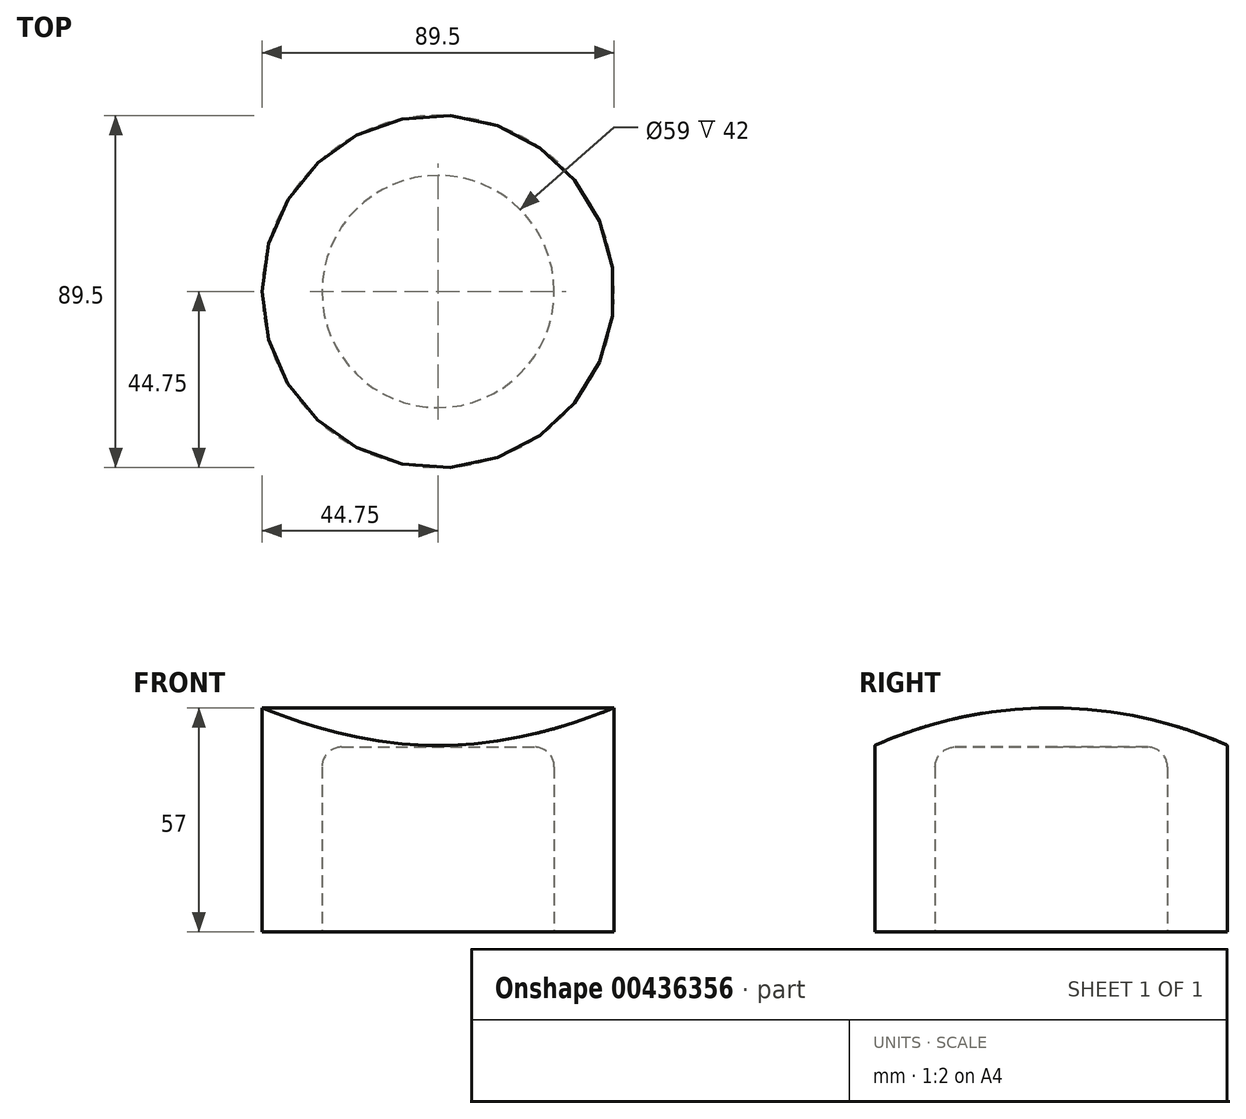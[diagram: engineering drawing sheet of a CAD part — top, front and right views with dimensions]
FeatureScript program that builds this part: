
annotation { "Feature Type Name" : "Feature", "Feature Type Description" : "" }
export const myFeature = defineFeature(function(context is Context, id is Id, definition is map)
    precondition{}
    {
        {
            var Q0;
            Q0=qCreatedBy(makeId("Front.planeOp"),FACE);
            var sketch = newSketch(context, id + "F0", { "sketchPlane" : qUnion([Q0])});
            skLineSegment(sketch, "E0", {"start": v(0, 0) * mm, "end": v(44.75, 0) * mm});
            skLineSegment(sketch, "E1", {"start": v(44.75, 0) * mm, "end": v(44.75, -57) * mm});
            skLineSegment(sketch, "E2", {"start": v(44.75, -57) * mm, "end": v(29.5, -57) * mm});
            skLineSegment(sketch, "E3", {"start": v(29.5, -57) * mm, "end": v(29.5, -48) * mm});
            skLineSegment(sketch, "E4", {"start": v(29.5, -48) * mm, "end": v(35.5, -48) * mm});
            skLineSegment(sketch, "E5", {"start": v(35.5, -51.58) * mm, "end": v(35.5, -48) * mm});
            skLineSegment(sketch, "E6", {"start": v(35.5, -51.58) * mm, "end": v(29.5, -51.58) * mm});
            skLineSegment(sketch, "E7", {"start": v(29.5, -51.58) * mm, "end": v(29.5, -15) * mm});
            skLineSegment(sketch, "E8", {"start": v(24.5, -10) * mm, "end": v(0, -10) * mm});
            skLineSegment(sketch, "E9", {"start": v(0, -10) * mm, "end": v(0, 0) * mm});
            skPoint(sketch, "E10.visualSharp", {"position": v(29.5, -10) * mm});
            skArc(sketch, "E10.filletArc", {"start": v(29.5, -15) * mm, "mid": v(28.04, -11.46) * mm, "end": v(24.5, -10) * mm});
            skSolve(sketch);
        }
        {
            var Q0;
            Q0 = qSketchRegion(id + "F0", true);
            var Q1;
            Q1=sQuery(id+"F0.wireOp",EDGE,"E9");
            revolve(context, id + "F1", {"entities" : qUnion([Q0]), "axis" : qUnion([Q1]), "revolveType" : RevolveType.FULL});
        }
        {
            var Q0;
            Q0=qCreatedBy(makeId("Right.planeOp"),FACE);
            var sketch = newSketch(context, id + "F2", { "sketchPlane" : qUnion([Q0])});
            skArc(sketch, "E11", {"start": v(-45.72, -10) * mm, "mid": v(0, 0) * mm, "end": v(45.72, -10) * mm});
            skLineSegment(sketch, "E12", {"start": v(-45.72, 0) * mm, "end": v(45.72, 0) * mm, "construction": true});
            skLineSegment(sketch, "E13", {"start": v(-45.72, -10) * mm, "end": v(-45.72, 10) * mm});
            skLineSegment(sketch, "E14", {"start": v(-45.72, 10) * mm, "end": v(45.72, 10) * mm});
            skLineSegment(sketch, "E15", {"start": v(45.72, 10) * mm, "end": v(45.72, -10) * mm});
            skLineSegment(sketch, "E16", {"start": v(0, 0) * mm, "end": v(0, 10) * mm, "construction": true});
            skSolve(sketch);
        }
        {
            var Q0;
            Q0 = qSketchRegion(id + "F2", true);
            extrude(context, id + "F3", {"entities" : qUnion([Q0]), "operationType" : NewBodyOperationType.REMOVE, "endBound" : BoundingType.SYMMETRIC, "oppositeDirection" : true, "depth" : 100 * mm});
        }
    });
